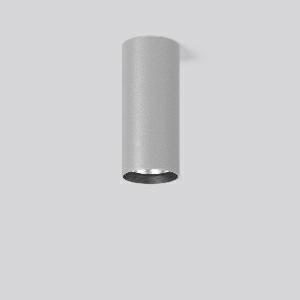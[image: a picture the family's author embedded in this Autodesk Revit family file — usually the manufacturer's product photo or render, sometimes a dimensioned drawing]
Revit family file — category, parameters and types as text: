
# Revit family: heledon_mini_a_931201_004_e443
name_source: partatom
category: Lighting Fixtures
units: mm (PartAtom-declared; Revit-internal decimal feet)

## family parameters
Cut with Voids When Loaded = No
Host = Face
Light Source = No
Part Type = Normal
Room Calculation Point = No
Round Connector Dimension = Use Diameter
Shared = No

## types (1)
- HELEDON mini A (1 x LED Modul 930, 2450 lm, 3000)
    Apparent Load = 20 VA
    Approval mark = CE
    CIE Flux Codes = 99 100 100 100 100
    Color Rendering = 90
    Color Temperature = 3000
    Default Elevation = 1800 mm
    Description = Series: HELEDON mini
Cylindrical surface-mounted downlight. Housing: die-cast aluminium, powder-coated. Internal ceiling frame polycarbonate with bayonet mounting. Black plastic ring and recessed LED to prevent glare from the side. Optical assembly with reflector made of MIRO-Silver with 98% total light reflection for outstanding efficiency - can be changed without tools. Best colour rendering index Ra>90. Suitable for Ceiling mounting. Easy installation with a separate ceiling frame with bayonet mounting and plug connection. Driver integrated. Connected via plug-in connector. High quality converter without flickering and stroboscopic effect. The following accessories can be mounted without use of tools: interchangeable lenses, decorative glasses, honeycomb louvre, clear and frosted diffusers, white interchangeable plastic ring. 
Colour: silver
Diameter: 87 mm
Height: 197 mm
Lamp: LED
Socket: without socket
Colour temperature: 3000K
Colour rendering index (CRI): 92
System power: 20 W
Rated luminous flux: 2450 lm
Luminous efficiency: 123 lm/W
Control gear: Regulated power supply
Protection class: I
Type of protection: IP 20
    Height = 197 mm
    Lamp = 1 x LED Modul 930
    Lamp Light Flux = 2450 lm
    Lamp count = 1
    Length = 87 mm
    Lifetime = 50000 h
    Luminous efficacy = 123 lm/W
    Manufacturer = RZB
    ModVariant = No
    Model = 931201.004
    Mounting Place = Ceiling
    Mounting Type = Surface mounted
    Number of Poles = 1
    OnlyDefault = Yes
    Power Factor = 1
    Product Name = HELEDON mini A
    Product group = Surface mounted downlights
    ProductGroupID = 302
    Protection Class = Protection class I
    Protection Degree = IP 20
    RLX_Detail_Level = 1
    RLX_Emergency_Light_Flux = 0 lm
    RLX_Emergency_Type = 0
    RLX_Emergency_Type_DB = No
    RlxData = <blob elided: 108253 chars, md5=38b4e91a>
    Socket = socket
    Standby Power = 0 W
    System Light Flux = 2450 lm
    System Power = 20 W
    Type Comments = Product without accessories
    Type Image = 931188.004.jpg
    URL = http://relux.com
    VarID = ---
    Voltage = 230 V
    Voltage Range = 220-240 V
    Weight = 0.00 kg
    Width = 0 mm  [stored 0 ft]

note: [stored X ft] marks values corroborated as IEEE doubles in the binary element streams (Revit-internal decimal feet)

## geometry (parser evidence)
native form markers: Blend x4, Sweep x8
no freeform markers — native parametric forms only
